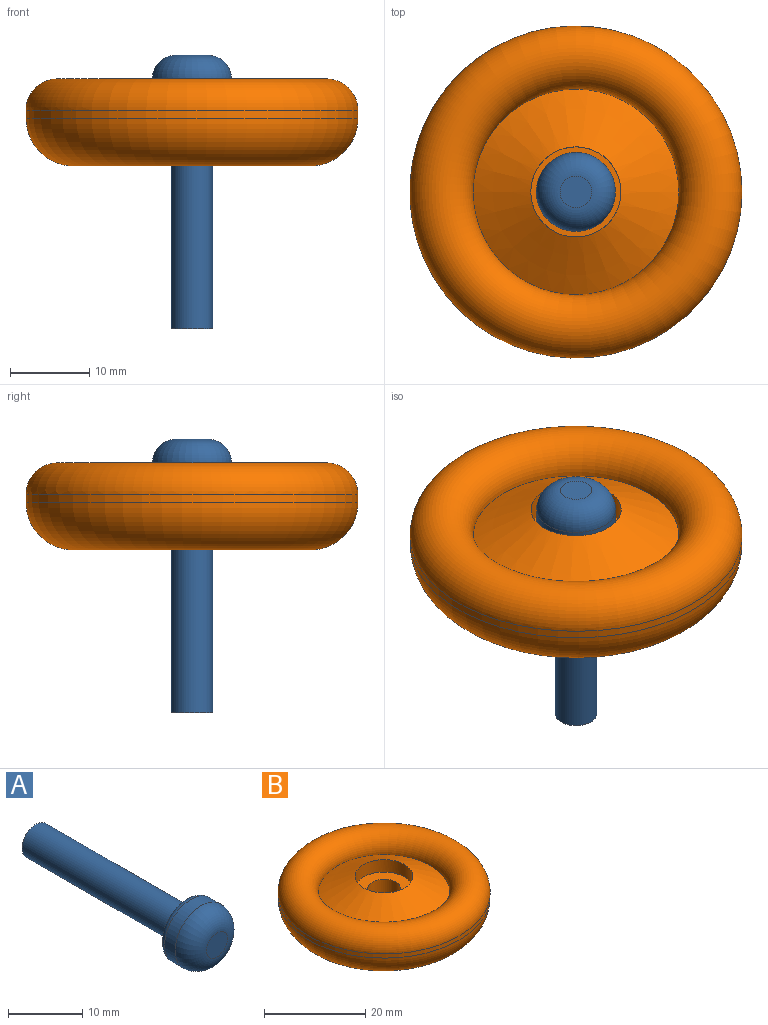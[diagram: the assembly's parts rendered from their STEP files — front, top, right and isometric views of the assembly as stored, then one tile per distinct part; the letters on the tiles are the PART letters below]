
ASSEMBLY  parts=2 mates=1
PART A: 7 faces, bbox 10.8x34.6x10.8 mm
  f0: plane 4x4mm, normal (0,-1,0), area 12.6mm2, adj f5
  f1: cylinder r=5mm len=10mm, axis (0,1,0), area 62.8mm2, adj f5,f6
  f2: cylinder r=2.62mm len=28.6mm, axis (0,1,0), area 471.7mm2, adj f3,f4
  f3: plane 8x8mm, normal (0,1,0), area 28.6mm2, adj f2,f6
  f4: plane 5.25x5.25mm, normal (0,1,0), area 21.6mm2, adj f2
  f5: torus R=2mm, axis (0,-1,0), area 115.8mm2, adj f0,f1
  f6: torus R=4mm, axis (0,-1,0), area 45.8mm2, adj f1,f3
PART B: 8 faces, bbox 45.5x45.5x11 mm
  f0: cylinder r=21mm len=42mm, axis (0,0,-1), area 131.9mm2, adj f2,f7
  f1: plane 30x30mm, normal (0,0,-1), area 673.7mm2, adj f3,f7
  f2: torus R=17mm, axis (0,0,1), area 1342.3mm2, adj f0,f6
  f3: cylinder r=3.25mm len=8mm, axis (0,0,-1), area 163.4mm2, adj f1,f4
  f4: plane 11.4x11.4mm, normal (0,0,1), area 68.9mm2, adj f3,f5
  f5: cylinder r=5.7mm len=11.4mm, axis (0,0,-1), area 107.4mm2, adj f4,f6
  f6: cone r=5.7mm half-angle=61.3deg, axis (0,0,-1), area 489mm2, adj f2,f5
  f7: torus R=15mm, axis (0,0,1), area 1114.5mm2, adj f0,f1
PLACE A rot(axis=(-1,0,0),90deg) t=(-4.52,-1.67,-24.69)mm
PLACE B t=(-4.52,-1.67,-4.09)mm
MATE cylindrical A.f2 <-> B.f3  axis (0,0,-1) through (-4.52,-1.67,-10.39)mm
